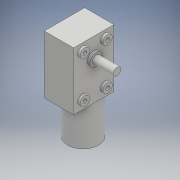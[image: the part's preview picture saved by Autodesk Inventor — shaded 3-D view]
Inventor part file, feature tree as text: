
AUTODESK INVENTOR PART (.ipt)
format: ipt  version: 2017 (Build 210142000, 142)  size: 169,472 bytes
history: native  units: mm
features: extrude x8, sketch x8, mirror x4, other x3
ambient origin geometry x8: Origin, YZ Plane, XZ Plane, XY Plane, X Axis, Y Axis, Z Axis, Center Point
bodies: Body1 (feature_tree)
feature tree (23):
  other  "Твердое тело1"
  extrude  "Выдавливание1"  Depth=24.4mm
  other  "РабПлоскость1"
  extrude  "Выдавливание2"  Depth=30.8mm TaperAngle=0.0deg
  extrude  "Выдавливание3"  Depth=46.0mm
  other  "РабПлоскость2"
  mirror  "Зеркальное отражение1"
  extrude  "Выдавливание4"  Depth=32.0mm
  mirror  "Зеркальное отражение2"
  extrude  "Выдавливание5"  Depth=23.2mm TaperAngle=0.0deg
  extrude  "Выдавливание6"  Depth=7.4mm
  mirror  "Зеркальное отражение3"
  extrude  "Выдавливание7"  Depth=12.8mm
  mirror  "Зеркальное отражение4"
  extrude  "Выдавливание8"  Depth=70.8mm
  sketch  "Эскиз1"
  sketch  "Эскиз2"
  sketch  "Эскиз3"
  sketch  "Эскиз4"
  sketch  "Эскиз5"
  sketch  "Эскиз6"
  sketch  "Эскиз8"
  sketch  "Эскиз9"
